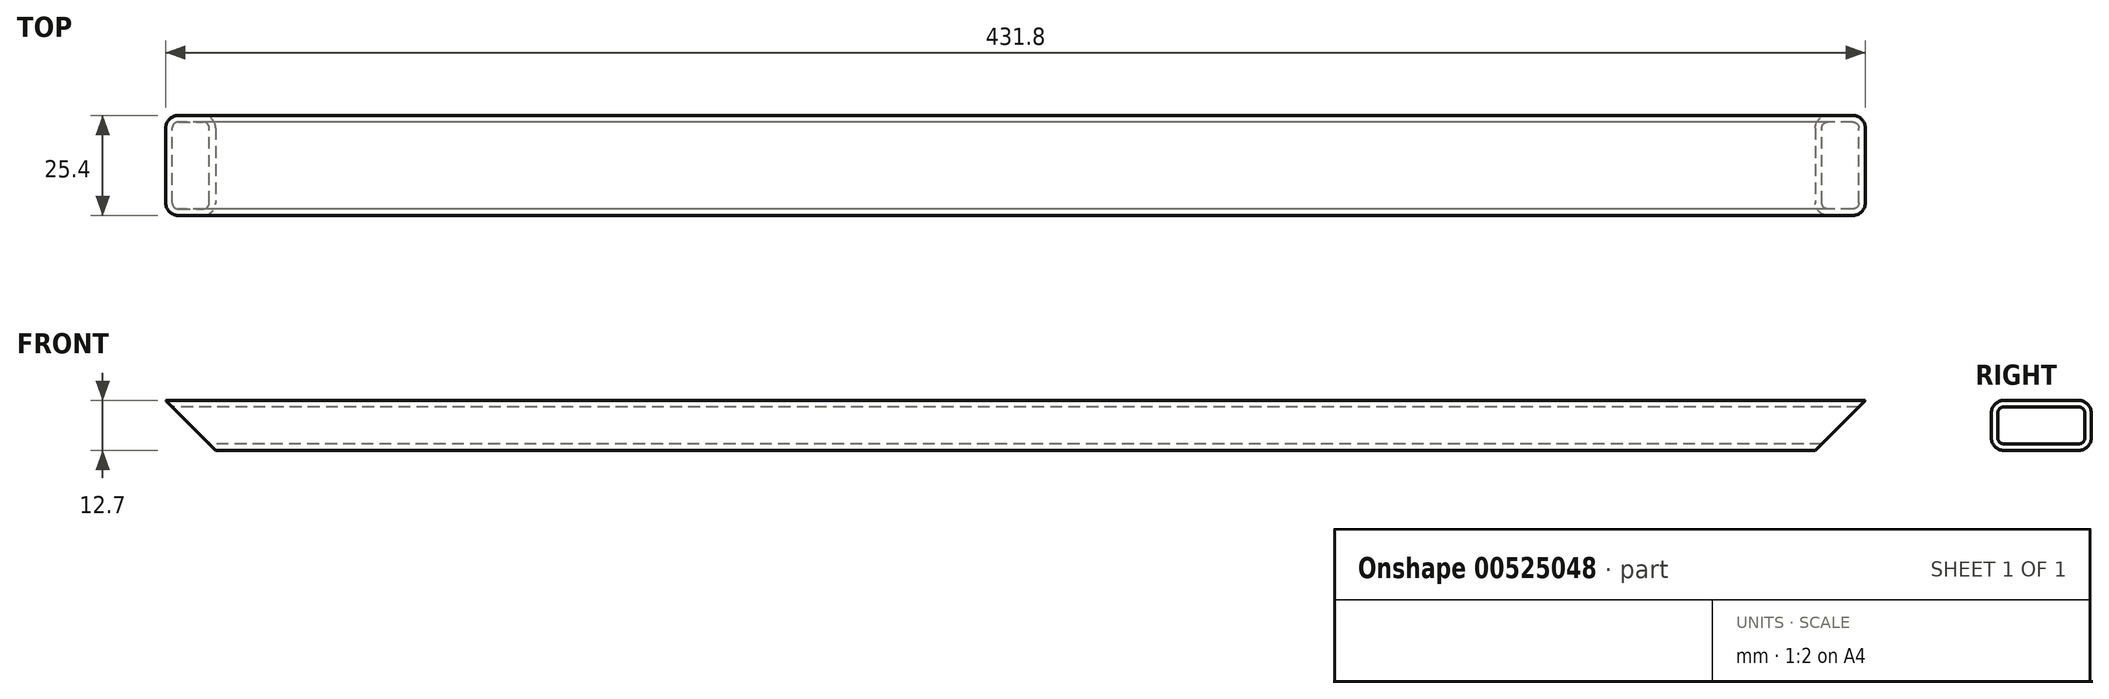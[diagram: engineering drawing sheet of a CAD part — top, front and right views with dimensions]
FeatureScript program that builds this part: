
annotation { "Feature Type Name" : "Feature", "Feature Type Description" : "" }
export const myFeature = defineFeature(function(context is Context, id is Id, definition is map)
    precondition{}
    {
        {
            var Q0;
            Q0=qCreatedBy(makeId("Right.planeOp"),FACE);
            var sketch = newSketch(context, id + "F0", { "sketchPlane" : qUnion([Q0])});
            skLineSegment(sketch, "E0.bottom", {"start": v(-9.53, 4.7) * mm, "end": v(9.53, 4.7) * mm});
            skLineSegment(sketch, "E0.top", {"start": v(-9.53, -4.7) * mm, "end": v(9.53, -4.7) * mm});
            skLineSegment(sketch, "E0.left", {"start": v(-11.05, 3.17) * mm, "end": v(-11.05, -3.18) * mm});
            skLineSegment(sketch, "E0.right", {"start": v(11.05, 3.18) * mm, "end": v(11.05, -3.18) * mm});
            skPoint(sketch, "E1.visualSharp", {"position": v(-11.05, 4.7) * mm});
            skArc(sketch, "E1.filletArc", {"start": v(-9.53, 4.7) * mm, "mid": v(-10.6, 4.25) * mm, "end": v(-11.05, 3.17) * mm});
            skPoint(sketch, "E2.visualSharp", {"position": v(-11.05, -4.7) * mm});
            skArc(sketch, "E2.filletArc", {"start": v(-11.05, -3.18) * mm, "mid": v(-10.6, -4.25) * mm, "end": v(-9.53, -4.7) * mm});
            skPoint(sketch, "E3.visualSharp", {"position": v(11.05, -4.7) * mm});
            skArc(sketch, "E3.filletArc", {"start": v(9.53, -4.7) * mm, "mid": v(10.6, -4.25) * mm, "end": v(11.05, -3.18) * mm});
            skPoint(sketch, "E4.visualSharp", {"position": v(11.05, 4.7) * mm});
            skArc(sketch, "E4.filletArc", {"start": v(11.05, 3.18) * mm, "mid": v(10.6, 4.25) * mm, "end": v(9.53, 4.7) * mm});
            skArc(sketch, "E5.0", {"start": v(-12.7, -3.18) * mm, "mid": v(-11.77, -5.42) * mm, "end": v(-9.53, -6.35) * mm});
            skLineSegment(sketch, "E5.1", {"start": v(-12.7, 3.18) * mm, "end": v(-12.7, -3.18) * mm});
            skLineSegment(sketch, "E5.2", {"start": v(-9.53, -6.35) * mm, "end": v(9.53, -6.35) * mm});
            skArc(sketch, "E5.3", {"start": v(-9.53, 6.35) * mm, "mid": v(-11.77, 5.42) * mm, "end": v(-12.7, 3.18) * mm});
            skArc(sketch, "E5.4", {"start": v(9.53, -6.35) * mm, "mid": v(11.77, -5.42) * mm, "end": v(12.7, -3.17) * mm});
            skLineSegment(sketch, "E5.5", {"start": v(12.7, 3.18) * mm, "end": v(12.7, -3.18) * mm});
            skArc(sketch, "E5.6", {"start": v(12.7, 3.17) * mm, "mid": v(11.77, 5.42) * mm, "end": v(9.53, 6.35) * mm});
            skLineSegment(sketch, "E5.7", {"start": v(-9.53, 6.35) * mm, "end": v(9.53, 6.35) * mm});
            skPoint(sketch, "E6", {"position": v(0, 4.7) * mm});
            skPoint(sketch, "E7", {"position": v(11.05, 0) * mm});
            skSolve(sketch);
        }
        {
            var Q0;
            Q0 = qSketchRegion(id + "F0", true);
            extrude(context, id + "F1", {"entities" : qUnion([Q0]), "endBound" : BoundingType.SYMMETRIC, "depth" : 431.8 * mm, "offsetDistance" : 25.4 * mm});
        }
        {
            var Q0;
            Q0=qCreatedBy(makeId("Front.planeOp"),FACE);
            var sketch = newSketch(context, id + "F2", { "sketchPlane" : qUnion([Q0])});
            skLineSegment(sketch, "E8", {"start": v(-215.9, -6.35) * mm, "end": v(-203.2, -6.35) * mm});
            skLineSegment(sketch, "E9", {"start": v(-203.2, -6.35) * mm, "end": v(-215.9, 6.35) * mm});
            skLineSegment(sketch, "E10", {"start": v(-215.9, 6.35) * mm, "end": v(-215.9, -6.35) * mm});
            skLineSegment(sketch, "E11", {"start": v(0, 0) * mm, "end": v(0, 18.5) * mm, "construction": true});
            skLineSegment(sketch, "E12.MirrorCS", {"start": v(215.9, -6.35) * mm, "end": v(203.2, -6.35) * mm});
            skLineSegment(sketch, "E13.MirrorCS", {"start": v(203.2, -6.35) * mm, "end": v(215.9, 6.35) * mm});
            skLineSegment(sketch, "E14.MirrorCS", {"start": v(215.9, 6.35) * mm, "end": v(215.9, -6.35) * mm});
            skSolve(sketch);
        }
        {
            var Q0;
            Q0 = qSketchRegion(id + "F2", true);
            extrude(context, id + "F3", {"entities" : qUnion([Q0]), "operationType" : NewBodyOperationType.REMOVE, "endBound" : BoundingType.THROUGH_ALL, "oppositeDirection" : true, "depth" : 25.4 * mm, "offsetDistance" : 25.4 * mm, "hasSecondDirection" : true, "secondDirectionBound" : SecondDirectionBoundingType.THROUGH_ALL, "secondDirectionOppositeDirection" : false, "secondDirectionDepth" : 25.4 * mm});
        }
    });
